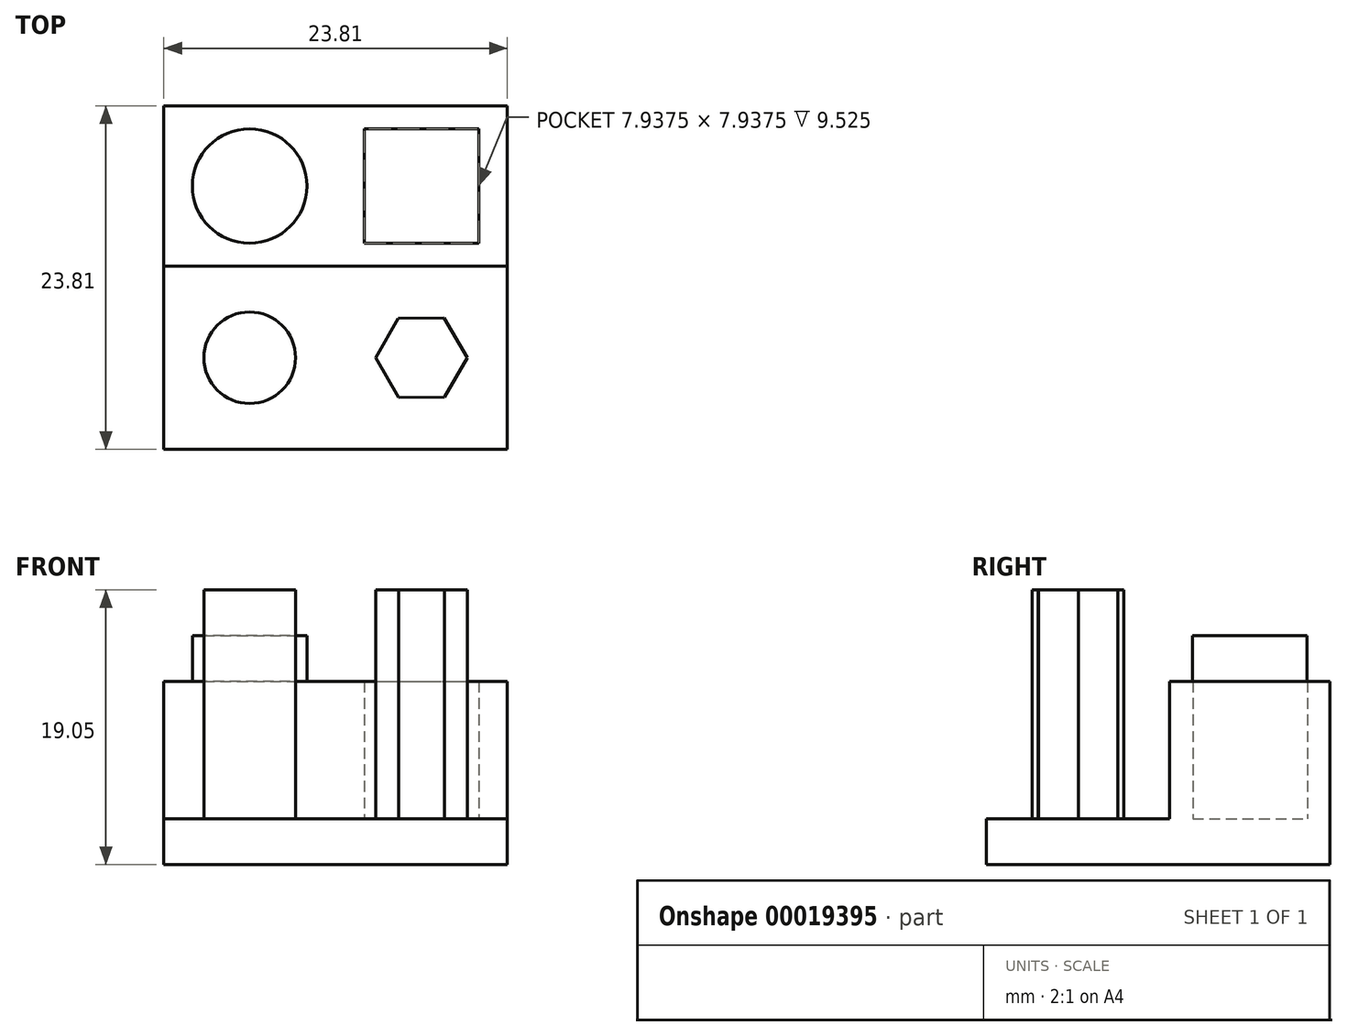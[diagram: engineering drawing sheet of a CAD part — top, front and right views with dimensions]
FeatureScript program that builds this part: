
annotation { "Feature Type Name" : "Feature", "Feature Type Description" : "" }
export const myFeature = defineFeature(function(context is Context, id is Id, definition is map)
    precondition{}
    {
        {
            var Q0;
            Q0=qCreatedBy(makeId("Top.planeOp"),FACE);
            var sketch = newSketch(context, id + "F0", { "sketchPlane" : qUnion([Q0])});
            skLineSegment(sketch, "E0.bottom", {"start": v(-13.9, 11.31) * mm, "end": v(9.91, 11.31) * mm});
            skLineSegment(sketch, "E0.top", {"start": v(-13.9, -12.5) * mm, "end": v(9.91, -12.5) * mm});
            skLineSegment(sketch, "E0.left", {"start": v(-13.9, 11.31) * mm, "end": v(-13.9, -12.5) * mm});
            skLineSegment(sketch, "E0.right", {"start": v(9.91, 11.31) * mm, "end": v(9.91, -12.5) * mm});
            skLineSegment(sketch, "E1", {"start": v(-13.9, 0.2) * mm, "end": v(9.91, 0.2) * mm});
            skLineSegment(sketch, "E2.0", {"start": v(0.78, -6.17) * mm, "end": v(2.36, -3.4) * mm});
            skLineSegment(sketch, "E2.1", {"start": v(2.36, -3.4) * mm, "end": v(5.54, -3.4) * mm});
            skLineSegment(sketch, "E2.2", {"start": v(5.54, -3.4) * mm, "end": v(7.13, -6.14) * mm});
            skLineSegment(sketch, "E2.3", {"start": v(7.13, -6.14) * mm, "end": v(5.56, -8.9) * mm});
            skLineSegment(sketch, "E2.4", {"start": v(5.56, -8.9) * mm, "end": v(2.38, -8.9) * mm});
            skLineSegment(sketch, "E2.5", {"start": v(2.38, -8.9) * mm, "end": v(0.78, -6.17) * mm});
            skPoint(sketch, "E2.0.midPoint", {"position": v(1.57, -4.79) * mm});
            skCircle(sketch, "E3", {"center": v(-7.95, -6.15) * mm, "radius": 3.18 * mm});
            skCircle(sketch, "E4", {"center": v(-7.95, 5.75) * mm, "radius": 3.97 * mm});
            skLineSegment(sketch, "E5.rect.bottom", {"start": v(0, 1.8) * mm, "end": v(7.94, 1.8) * mm});
            skLineSegment(sketch, "E5.rect.top", {"start": v(0, 9.73) * mm, "end": v(7.94, 9.73) * mm});
            skLineSegment(sketch, "E5.rect.left", {"start": v(0, 1.8) * mm, "end": v(0, 9.73) * mm});
            skLineSegment(sketch, "E5.rect.right", {"start": v(7.94, 1.8) * mm, "end": v(7.94, 9.73) * mm});
            skPoint(sketch, "E5.rect.middle", {"position": v(3.97, 5.76) * mm});
            skSolve(sketch);
        }
        {
            var Q0;
            {var subQ2=sQuery(id+"F0.wireOp",EDGE,"E0.top");Q0=makeQuery(id+"F0.imprint","IMPRINT",FACE,{"disambiguationData":[TD([[makeQuery(id+"F0.imprint","IMPRINT",EDGE,{"derivedFrom":subQ2}),1.0]])]});}
            extrude(context, id + "F1", {"entities" : qUnion([Q0]), "depth" : 3.17 * mm});
        }
        {
            var Q0;
            Q0=makeQuery(id+"F0.imprint","IMPRINT",FACE,{"disambiguationData":[TD([[makeQuery(id+"F0.imprint","IMPRINT",EDGE,{"derivedFrom":sQuery(id+"F0.wireOp",EDGE,"E3")}),1.0]])]});
            var Q1;
            Q1=makeQuery(id+"F0.imprint","IMPRINT",FACE,{"disambiguationData":[TD([[makeQuery(id+"F0.imprint","IMPRINT",EDGE,{"derivedFrom":sQuery(id+"F0.wireOp",EDGE,"E2.0")}),-1.0]])]});
            extrude(context, id + "F2", {"entities" : qUnion([Q0, Q1]), "operationType" : NewBodyOperationType.ADD, "depth" : 19.05 * mm});
        }
        {
            var Q0;
            {var subQ2=sQuery(id+"F0.wireOp",EDGE,"E0.bottom");Q0=makeQuery(id+"F0.imprint","IMPRINT",FACE,{"disambiguationData":[TD([[makeQuery(id+"F0.imprint","IMPRINT",EDGE,{"derivedFrom":subQ2}),-1.0]])]});}
            extrude(context, id + "F3", {"entities" : qUnion([Q0]), "operationType" : NewBodyOperationType.ADD, "depth" : 12.7 * mm});
        }
        {
            var Q0;
            Q0=makeQuery(id+"F0.imprint","IMPRINT",FACE,{"disambiguationData":[TD([[makeQuery(id+"F0.imprint","IMPRINT",EDGE,{"derivedFrom":sQuery(id+"F0.wireOp",EDGE,"E5.rect.bottom")}),1.0]])]});
            extrude(context, id + "F4", {"entities" : qUnion([Q0]), "operationType" : NewBodyOperationType.ADD, "depth" : 3.17 * mm});
        }
        {
            var Q0;
            Q0=makeQuery(id+"F0.imprint","IMPRINT",FACE,{"disambiguationData":[TD([[makeQuery(id+"F0.imprint","IMPRINT",EDGE,{"derivedFrom":sQuery(id+"F0.wireOp",EDGE,"E4")}),1.0]])]});
            extrude(context, id + "F5", {"entities" : qUnion([Q0]), "operationType" : NewBodyOperationType.ADD, "depth" : 15.88 * mm});
        }
    });
